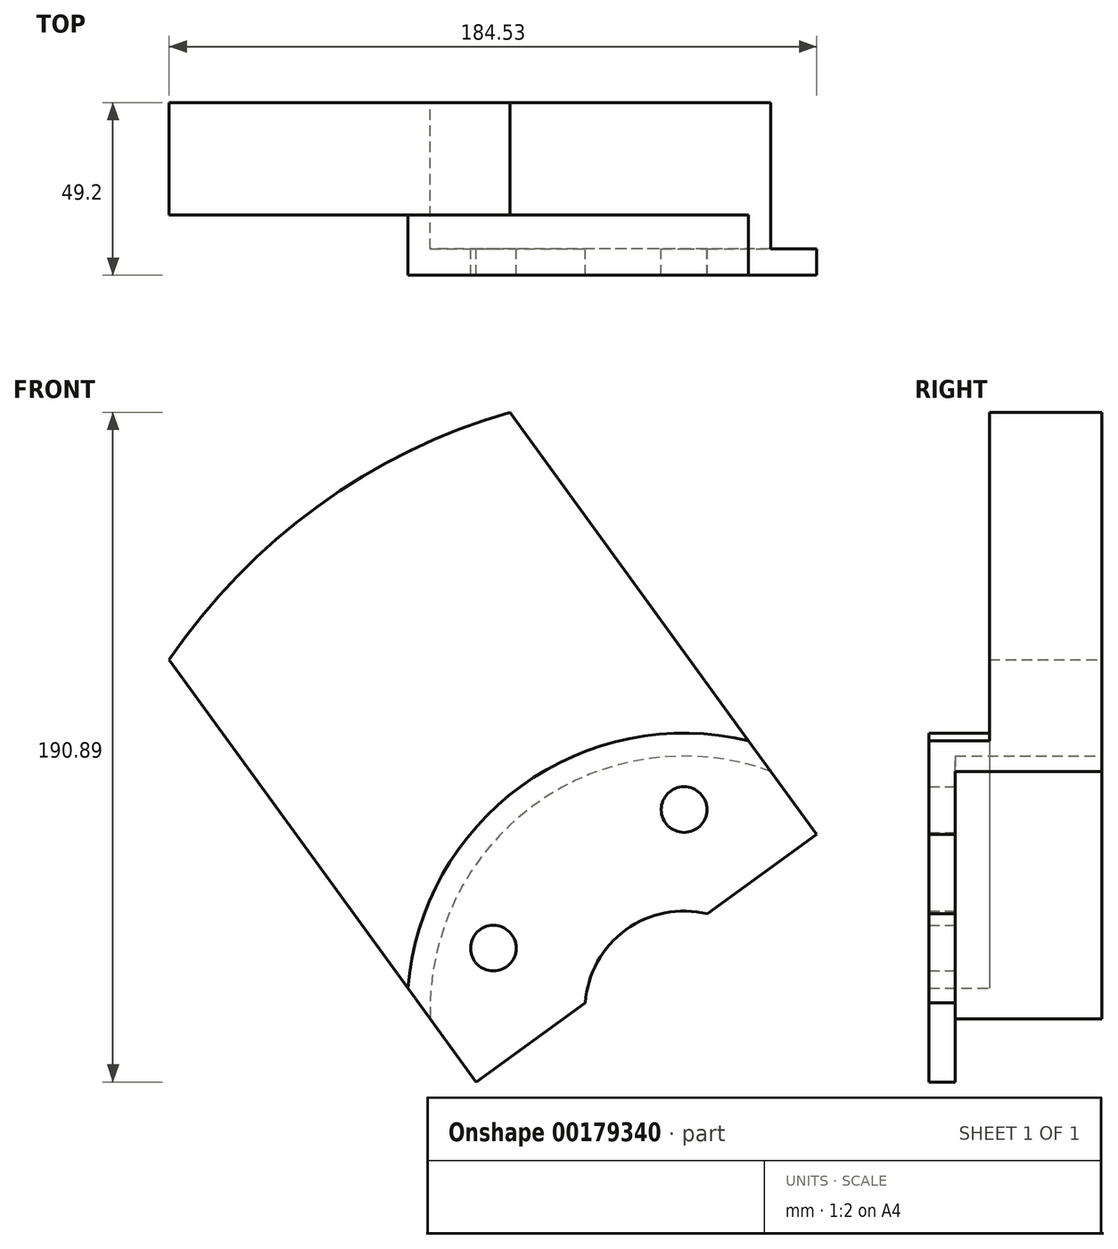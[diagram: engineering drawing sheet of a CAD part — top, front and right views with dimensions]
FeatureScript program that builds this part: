
annotation { "Feature Type Name" : "Feature", "Feature Type Description" : "" }
export const myFeature = defineFeature(function(context is Context, id is Id, definition is map)
    precondition{}
    {
        {
            var Q0;
            Q0=qCreatedBy(makeId("Front.planeOp"),FACE);
            var sketch = newSketch(context, id + "F0", { "sketchPlane" : qUnion([Q0])});
            skArc(sketch, "E0", {"start": v(-49.65, 170.41) * mm, "mid": v(-104.33, 143.6) * mm, "end": v(-146.73, 99.88) * mm});
            skArc(sketch, "E1", {"start": v(24.74, 68.03) * mm, "mid": v(-42.55, 58.56) * mm, "end": v(-72.35, -2.5) * mm});
            skArc(sketch, "E2", {"start": v(18.4, 76.77) * mm, "mid": v(-46.4, 63.86) * mm, "end": v(-78.7, 6.23) * mm});
            skCircle(sketch, "E3", {"center": v(0, 57.15) * mm, "radius": 6.5 * mm});
            skArc(sketch, "E4", {"start": v(33.07, 46.61) * mm, "mid": v(-33.6, 46.24) * mm, "end": v(-54.55, -17.04) * mm, "construction": true});
            skArc(sketch, "E5", {"start": v(6.69, 27.45) * mm, "mid": v(-16.6, 22.85) * mm, "end": v(-28.17, 2.12) * mm});
            skCircle(sketch, "E6.1.0", {"center": v(-54.35, 17.66) * mm, "radius": 6.5 * mm});
            skLineSegment(sketch, "E7", {"start": v(0, 0) * mm, "end": v(-104.33, 143.6) * mm, "construction": true});
            skLineSegment(sketch, "E8", {"start": v(-54.35, 17.66) * mm, "end": v(0, 57.15) * mm, "construction": true});
            skLineSegment(sketch, "E9", {"start": v(6.69, 27.45) * mm, "end": v(37.8, 50.05) * mm});
            skLineSegment(sketch, "E10", {"start": v(37.8, 50.05) * mm, "end": v(-49.65, 170.41) * mm});
            skLineSegment(sketch, "E11", {"start": v(-146.73, 99.88) * mm, "end": v(-59.28, -20.48) * mm});
            skLineSegment(sketch, "E12", {"start": v(-59.28, -20.48) * mm, "end": v(-28.17, 2.12) * mm});
            skSolve(sketch);
        }
        {
            var Q0;
            {var subQ0=sQuery(id+"F0.wireOp",EDGE,"E1");Q0=makeQuery(id+"F0.imprint","IMPRINT",FACE,{"disambiguationData":[TD([[makeQuery(id+"F0.imprint","IMPRINT",EDGE,{"derivedFrom":subQ0}),-1.0]])]});}
            var Q1;
            {var subQ1=sQuery(id+"F0.wireOp",EDGE,"E1");Q1=makeQuery(id+"F0.imprint","IMPRINT",FACE,{"disambiguationData":[TD([[makeQuery(id+"F0.imprint","IMPRINT",EDGE,{"derivedFrom":subQ1}),1.0]])]});}
            extrude(context, id + "F1", {"entities" : qUnion([Q0, Q1]), "depth" : 49.2 * mm});
        }
        {
            var Q0;
            {var subQ0=sQuery(id+"F0.wireOp",EDGE,"E0");Q0=makeQuery(id+"F0.imprint","IMPRINT",FACE,{"disambiguationData":[TD([[makeQuery(id+"F0.imprint","IMPRINT",EDGE,{"derivedFrom":subQ0}),1.0]])]});}
            extrude(context, id + "F2", {"entities" : qUnion([Q0]), "operationType" : NewBodyOperationType.ADD, "depth" : 32 * mm});
        }
        {
            var Q0;
            {var subQ1=sQuery(id+"F0.wireOp",EDGE,"E1");Q0=makeQuery(id+"F0.imprint","IMPRINT",FACE,{"disambiguationData":[TD([[makeQuery(id+"F0.imprint","IMPRINT",EDGE,{"derivedFrom":subQ1}),1.0]])]});}
            extrude(context, id + "F3", {"entities" : qUnion([Q0]), "operationType" : NewBodyOperationType.REMOVE, "depth" : 49.2 * mm - 7.5 * mm});
        }
    });
